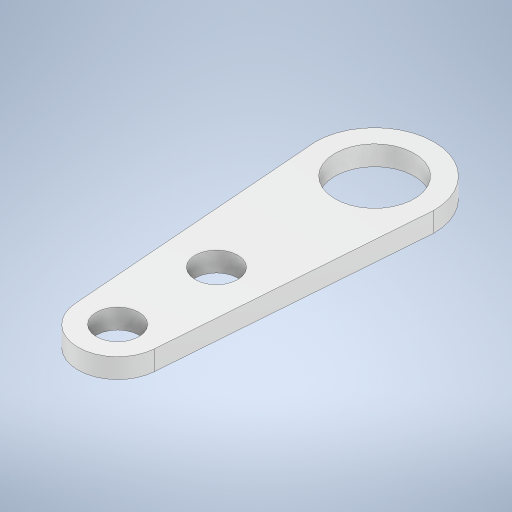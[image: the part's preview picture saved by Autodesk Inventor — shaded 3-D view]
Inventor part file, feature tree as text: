
AUTODESK INVENTOR PART (.ipt)
format: ipt  version: 2023 (Build 270158000, 158)  size: 250,368 bytes
history: native  units: mm
features: extrude x1, sketch x1
ambient origin geometry x8: Origin, YZ Plane, XZ Plane, XY Plane, X Axis, Y Axis, Z Axis, Center Point
bodies: Solid1 (feature_tree)
feature tree (2):
  extrude  "Extrusion1"  Depth=8.0mm
  sketch  "Sketch1"  dims[d0=6.0mm d1=8.0mm d2=2.15mm d3=5.0mm d4=2.15mm d5=4.0mm d6=4.0mm d7=1.0mm d8=0.0mm]
